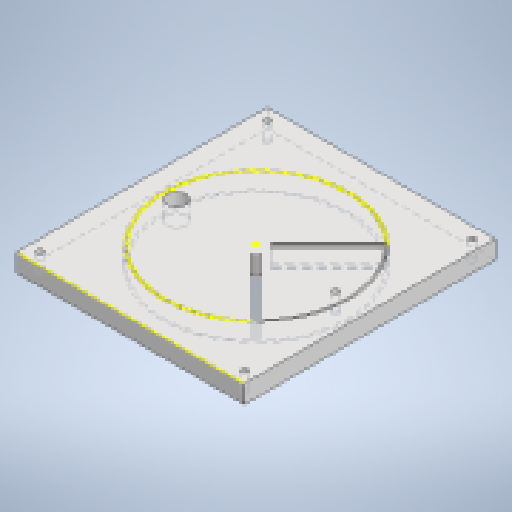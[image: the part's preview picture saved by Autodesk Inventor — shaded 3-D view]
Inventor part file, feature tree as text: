
AUTODESK INVENTOR PART (.ipt)
format: ipt  version: 2023 (Build 270158000, 158)  size: 352,768 bytes
history: native  units: mm
features: extrude x8, sketch x7, projected_geometry x1
ambient origin geometry x8: Origin, YZ Plane, XZ Plane, XY Plane, X Axis, Y Axis, Z Axis, Center Point
bodies: Solid1 (feature_tree)
feature tree (16):
  extrude  "Extrusion1"  Depth=110.0mm
  extrude  "Extrusion2"  TaperAngle=0.0deg  [1 undecoded]
  extrude  "Extrusion5"  Depth=150.0mm
  extrude  "Extrusion6"  Depth=8.0mm
  extrude  "Extrusion7"  Depth=5.0mm
  extrude  "Extrusion8"  Depth=5.0mm
  extrude  "Extrusion9"  Depth=55.0mm
  extrude  "Extrusion10"  Depth=10.0mm
  sketch  "Sketch1"  dims[d0=100.0mm d1=110.0mm]
  sketch  "Sketch8"  dims[d2=0.0mm d3=0.0mm]
  sketch  "Sketch9"  dims[d4=150.0mm d5=150.0mm]
  sketch  "Sketch10"  dims[d6=8.0mm d7=0.0mm d18=45.0mm d19=45.0mm d21=47.0mm d22=47.0mm]
  sketch  "Sketch11"  dims[d85=20.0mm d86=0.0mm d118=5.0mm]
  projected_geometry  "Projected Loop1"
  sketch  "Sketch12"  dims[d119=5.0mm d120=2.65mm]
  sketch  "Sketch13"  dims[d132=50.0mm d133=55.0mm d134=10.0mm d135=80.0mm d136=82.0mm d145=35.0mm d146=0.0mm d147=2.75mm d153=20.0mm d154=0.0mm d155=8.0mm d156=35.0mm d157=45.0deg d158=0.5mm d159=0.5mm d160=1.0mm d161=1.0mm d162=20.0mm d164=90.0deg d166=1.0mm d167=1.0mm d168=1.0mm d169=30.0mm d170=10.0mm d171=3.0mm d172=5.0mm d173=3.5mm d174=1.0mm d175=3.5mm d176=30.0mm d177=15.0mm d178=4.0mm d179=20.0mm d180=0.0mm d181=8.0mm d182=0.0mm d184=10.0mm d185=5.0mm d186=20.0mm d187=1.0mm d188=2.0mm d189=1.0mm d190=0.0mm d191=135.0deg d192=0.707107mm d193=0.707107mm d194=0.707107mm d195=0.707107mm d196=8.0mm d197=0.0mm d198=8.0mm d199=0.0mm d200=3.0mm d201=4.0mm d202=4.0mm d203=38.0mm d204=0.0mm]
note: 1 required parameter value undecoded (feature->parameter linkage not recoverable at this tier; creation-order binding heuristic only, values carry confidence <= 0.55)
